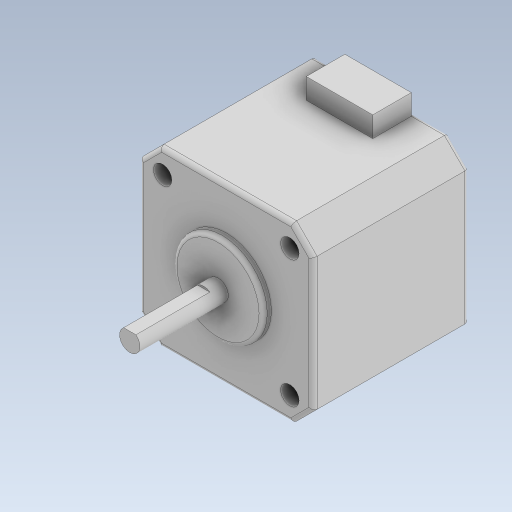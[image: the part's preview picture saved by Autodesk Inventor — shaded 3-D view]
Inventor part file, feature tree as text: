
AUTODESK INVENTOR PART (.ipt)
format: ipt  version: 2023 (Build 270158000, 158)  size: 203,264 bytes
history: native  units: in
note: dims shown in document units (in); Inventor stores cm internally (conversion verified against a paired STEP export)
features: extrude x6, sketch x6, fillet x1, projected_geometry x1
ambient origin geometry x8: Origin, YZ Plane, XZ Plane, XY Plane, X Axis, Y Axis, Z Axis, Center Point
bodies: Solid1 (feature_tree)
feature tree (14):
  extrude  "Extrusion1"  Depth=1.6654in
  extrude  "Extrusion2"  Depth=0.1969in
  extrude  "Extrusion3"  Depth=0.1969in
  fillet  "Fillet1"  Radius=0.1969in
  extrude  "Extrusion4"  Depth=0.1969in
  extrude  "Extrusion5"  Depth=1.4961in TaperAngle=0.0deg
  extrude  "Extrusion6"  Depth=0.1969in
  sketch  "Sketch1"  dims[d0=1.6654in d1=1.6654in]
  sketch  "Sketch2"  dims[d2=0.1969in d3=0.1969in]
  sketch  "Sketch3"  dims[d4=0.1969in d5=0.1969in d6=0.1969in]
  sketch  "Sketch4"  dims[d7=0.1969in d8=0.1969in]
  sketch  "Sketch5"  dims[d9=0.1969in d10=1.4961in d11=0.0in]
  projected_geometry  "Projected Loop1"
  sketch  "Sketch6"  dims[d12=1.2205in d13=0.1772in d14=0.3937in d15=0.0in d16=0.8661in d17=0.0787in d18=0.0in d19=0.0394in d20=0.1969in d21=0.9252in d22=0.0in d23=0.0787in d24=0.7087in d25=0.0in d26=0.6378in d27=0.3701in d28=0.1969in d29=0.0in]
